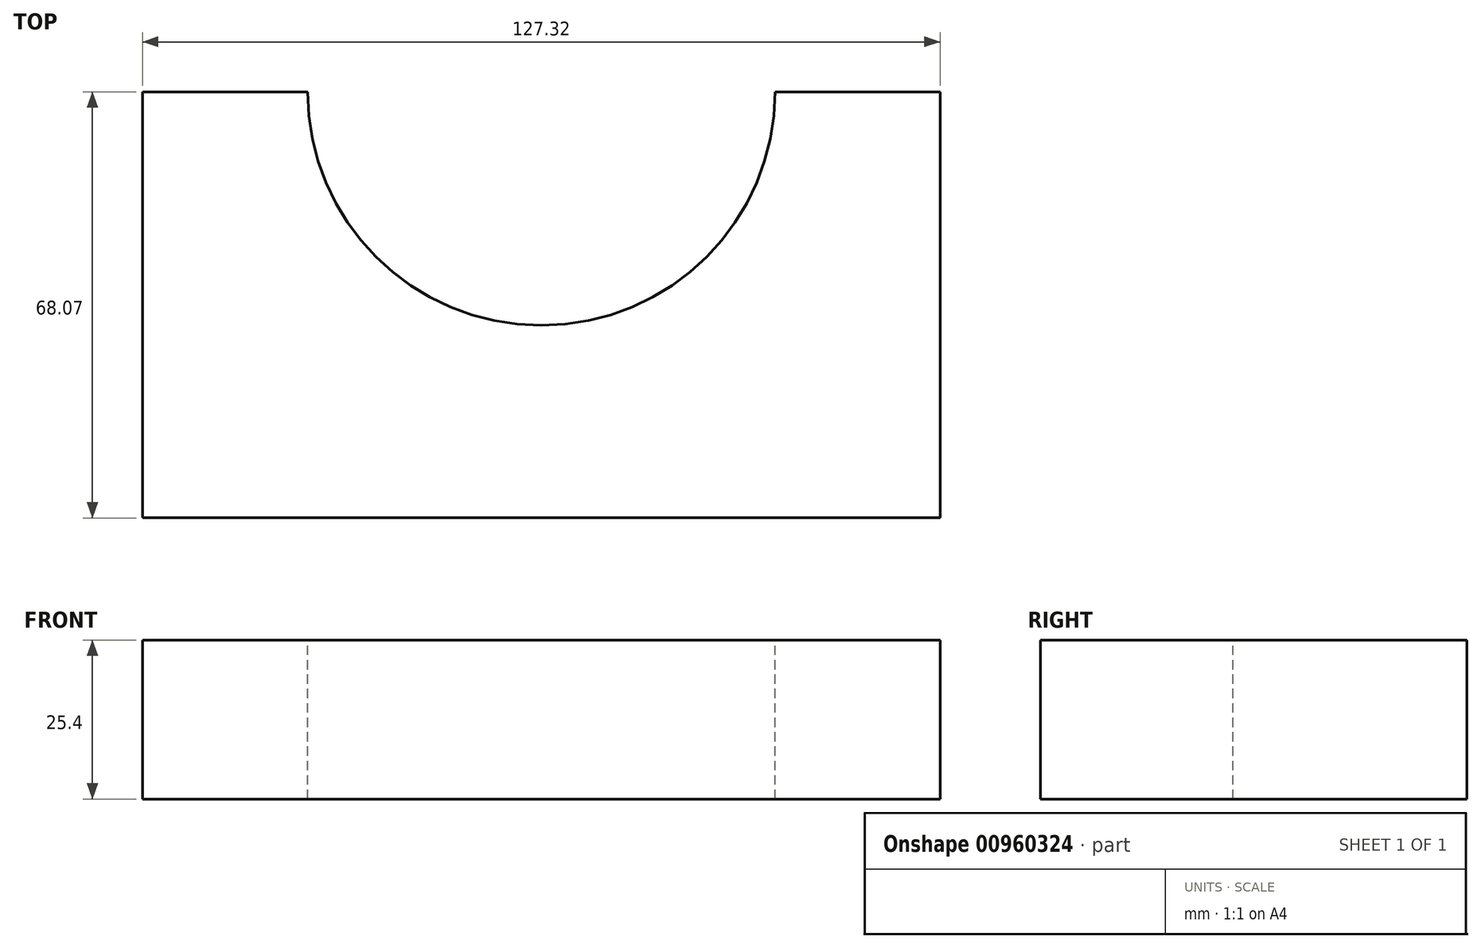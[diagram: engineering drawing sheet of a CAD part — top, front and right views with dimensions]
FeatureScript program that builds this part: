
annotation { "Feature Type Name" : "Feature", "Feature Type Description" : "" }
export const myFeature = defineFeature(function(context is Context, id is Id, definition is map)
    precondition{}
    {
        {
            var Q0;
            Q0=qCreatedBy(makeId("Top.planeOp"),FACE);
            var sketch = newSketch(context, id + "F0", { "sketchPlane" : qUnion([Q0])});
            skLineSegment(sketch, "E0.bottom", {"start": v(-60.1, 23.39) * mm, "end": v(67.23, 23.39) * mm});
            skLineSegment(sketch, "E0.top", {"start": v(-60.1, -44.68) * mm, "end": v(67.23, -44.68) * mm});
            skLineSegment(sketch, "E0.left", {"start": v(-60.1, 23.39) * mm, "end": v(-60.1, -44.68) * mm});
            skLineSegment(sketch, "E0.right", {"start": v(67.23, 23.39) * mm, "end": v(67.23, -44.68) * mm});
            skCircle(sketch, "E1", {"center": v(3.57, 23.39) * mm, "radius": 37.3 * mm});
            skSolve(sketch);
        }
        {
            var Q0;
            Q0=makeQuery(id+"F0.imprint","IMPRINT",FACE,{"disambiguationData":[TD([[makeQuery(id+"F0.imprint","IMPRINT",EDGE,{"derivedFrom":sQuery(id+"F0.wireOp",EDGE,"E0.top")}),1.0]])]});
            var Q1;
            {var subQ0=sQuery(id+"F0.wireOp",EDGE,"E1");var subQ1=sQuery(id+"F0.wireOp",EDGE,"E0.bottom");var subQ2=makeQuery(id+"F0.imprint","INTERSECT",VERTEX,{"disambiguationData":[OD(0.0)],"derivedFrom":[subQ1,subQ0]});Q1=makeQuery(id+"F0.imprint","IMPRINT",FACE,{"disambiguationData":[TD([[makeQuery(id+"F0.imprint","IMPRINT",EDGE,{"disambiguationData":[TD([[subQ2,-1.0]])],"derivedFrom":subQ1}),1.0]])]});}
            extrude(context, id + "F1", {"entities" : qUnion([Q0, Q1]), "oppositeDirection" : true, "depth" : 25.4 * mm, "offsetDistance" : 25.4 * mm});
        }
    });
